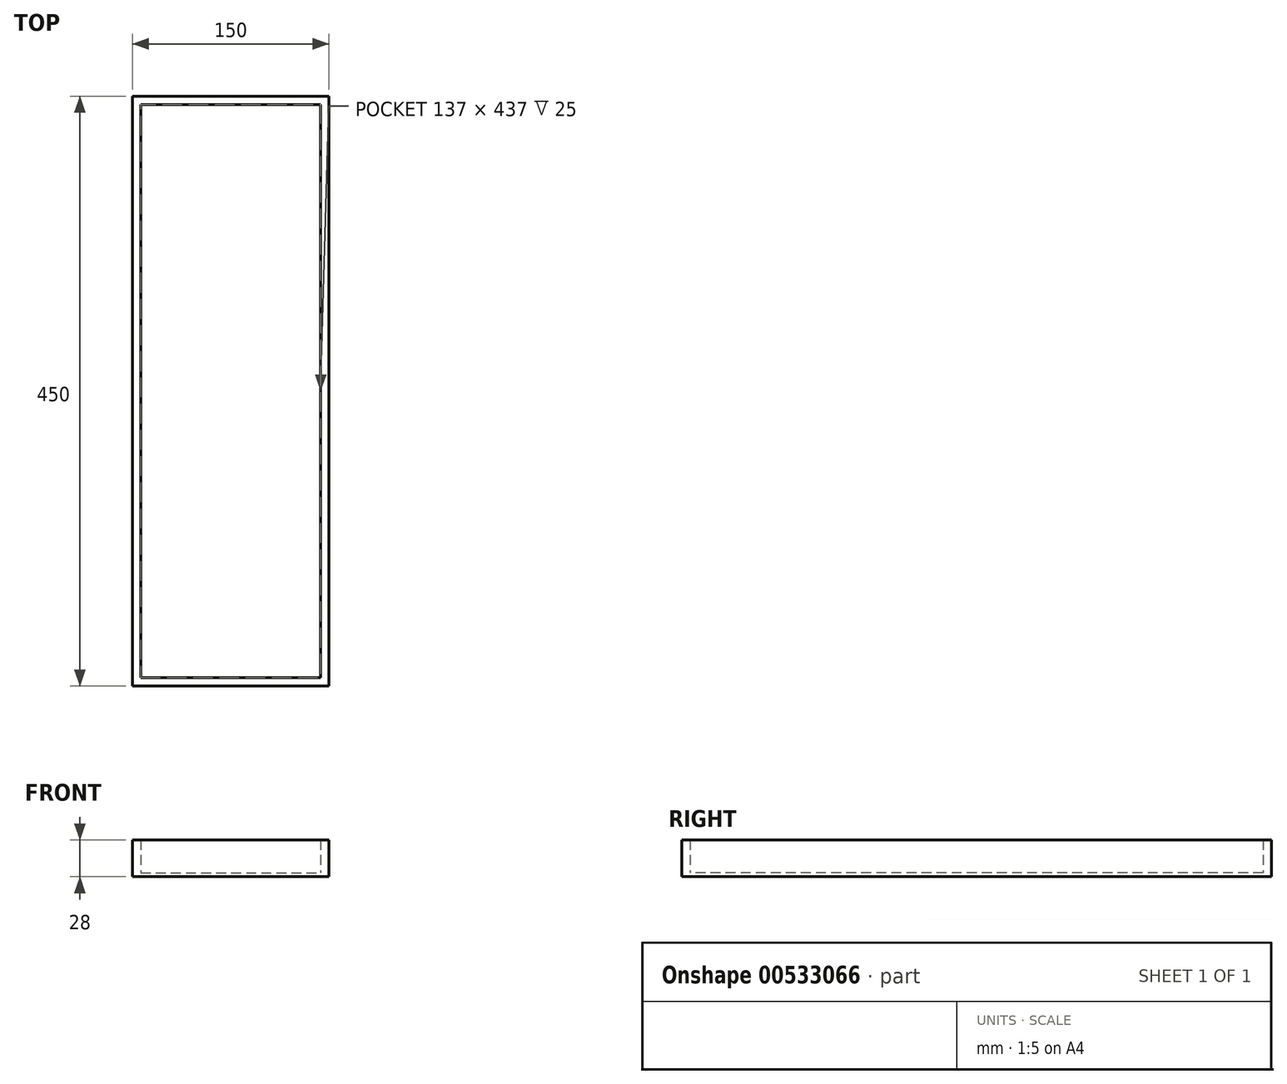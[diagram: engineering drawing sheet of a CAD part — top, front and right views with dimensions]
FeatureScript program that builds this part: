
annotation { "Feature Type Name" : "Feature", "Feature Type Description" : "" }
export const myFeature = defineFeature(function(context is Context, id is Id, definition is map)
    precondition{}
    {
        {
            var Q0;
            Q0=qCreatedBy(makeId("Top.planeOp"),FACE);
            var sketch = newSketch(context, id + "F0", { "sketchPlane" : qUnion([Q0])});
            skLineSegment(sketch, "E0.bottom", {"start": v(-94.98, 233) * mm, "end": v(55.02, 233) * mm});
            skLineSegment(sketch, "E0.top", {"start": v(-94.98, -217) * mm, "end": v(55.02, -217) * mm});
            skLineSegment(sketch, "E0.left", {"start": v(-94.98, 233) * mm, "end": v(-94.98, -217) * mm});
            skLineSegment(sketch, "E0.right", {"start": v(55.02, 233) * mm, "end": v(55.02, -217) * mm});
            skSolve(sketch);
        }
        {
            var Q0;
            Q0=makeQuery(id+"F0.imprint","IMPRINT",FACE,{"disambiguationData":[TD([[makeQuery(id+"F0.imprint","IMPRINT",EDGE,{"derivedFrom":sQuery(id+"F0.wireOp",EDGE,"E0.bottom")}),-1.0]])]});
            extrude(context, id + "F1", {"entities" : qUnion([Q0]), "depth" : 3 * mm, "offsetDistance" : 25 * mm});
        }
        {
            var Q0;
            Q0=makeQuery(id+"F1.opExtrude","CAP_FACE",FACE,{"disambiguationData":[OSD([sQuery(id+"F0.wireOp",EDGE,"E0.bottom"),sQuery(id+"F0.wireOp",EDGE,"E0.top"),sQuery(id+"F0.wireOp",EDGE,"E0.left"),sQuery(id+"F0.wireOp",EDGE,"E0.right")])],"isStart":false});
            var sketch = newSketch(context, id + "F2", { "sketchPlane" : qUnion([Q0])});
            skLineSegment(sketch, "E1.top", {"start": v(-94.98, -217) * mm, "end": v(55.02, -217) * mm});
            skLineSegment(sketch, "E1.left", {"start": v(-94.98, 233) * mm, "end": v(-94.98, -217) * mm});
            skLineSegment(sketch, "E1.right", {"start": v(55.02, 233) * mm, "end": v(55.02, -217) * mm});
            skLineSegment(sketch, "E2.bottom", {"start": v(-88.48, 226.5) * mm, "end": v(48.52, 226.5) * mm});
            skLineSegment(sketch, "E2.top", {"start": v(-88.48, -210.5) * mm, "end": v(48.52, -210.5) * mm});
            skLineSegment(sketch, "E2.left", {"start": v(-88.48, 226.5) * mm, "end": v(-88.48, -210.5) * mm});
            skLineSegment(sketch, "E2.right", {"start": v(48.52, 226.5) * mm, "end": v(48.52, -210.5) * mm});
            skLineSegment(sketch, "E3.bottom", {"start": v(48.52, 73.86) * mm, "end": v(55.02, 73.86) * mm});
            skLineSegment(sketch, "E3.top", {"start": v(48.52, 73.86) * mm, "end": v(55.02, 73.86) * mm});
            skLineSegment(sketch, "E3.left", {"start": v(48.52, 73.86) * mm, "end": v(48.52, 73.86) * mm});
            skLineSegment(sketch, "E3.right", {"start": v(55.02, 73.86) * mm, "end": v(55.02, 73.86) * mm});
            skSolve(sketch);
        }
        {
            var Q0;
            {var subQ1=sQuery(id+"F2.wireOp",EDGE,"E1.top");Q0=makeQuery(id+"F2.imprint","IMPRINT",FACE,{"disambiguationData":[TD([[makeQuery(id+"F2.imprint","IMPRINT",EDGE,{"derivedFrom":subQ1}),1.0]])]});}
            extrude(context, id + "F3", {"entities" : qUnion([Q0]), "operationType" : NewBodyOperationType.ADD, "depth" : 25 * mm, "offsetDistance" : 25 * mm});
        }
    });
